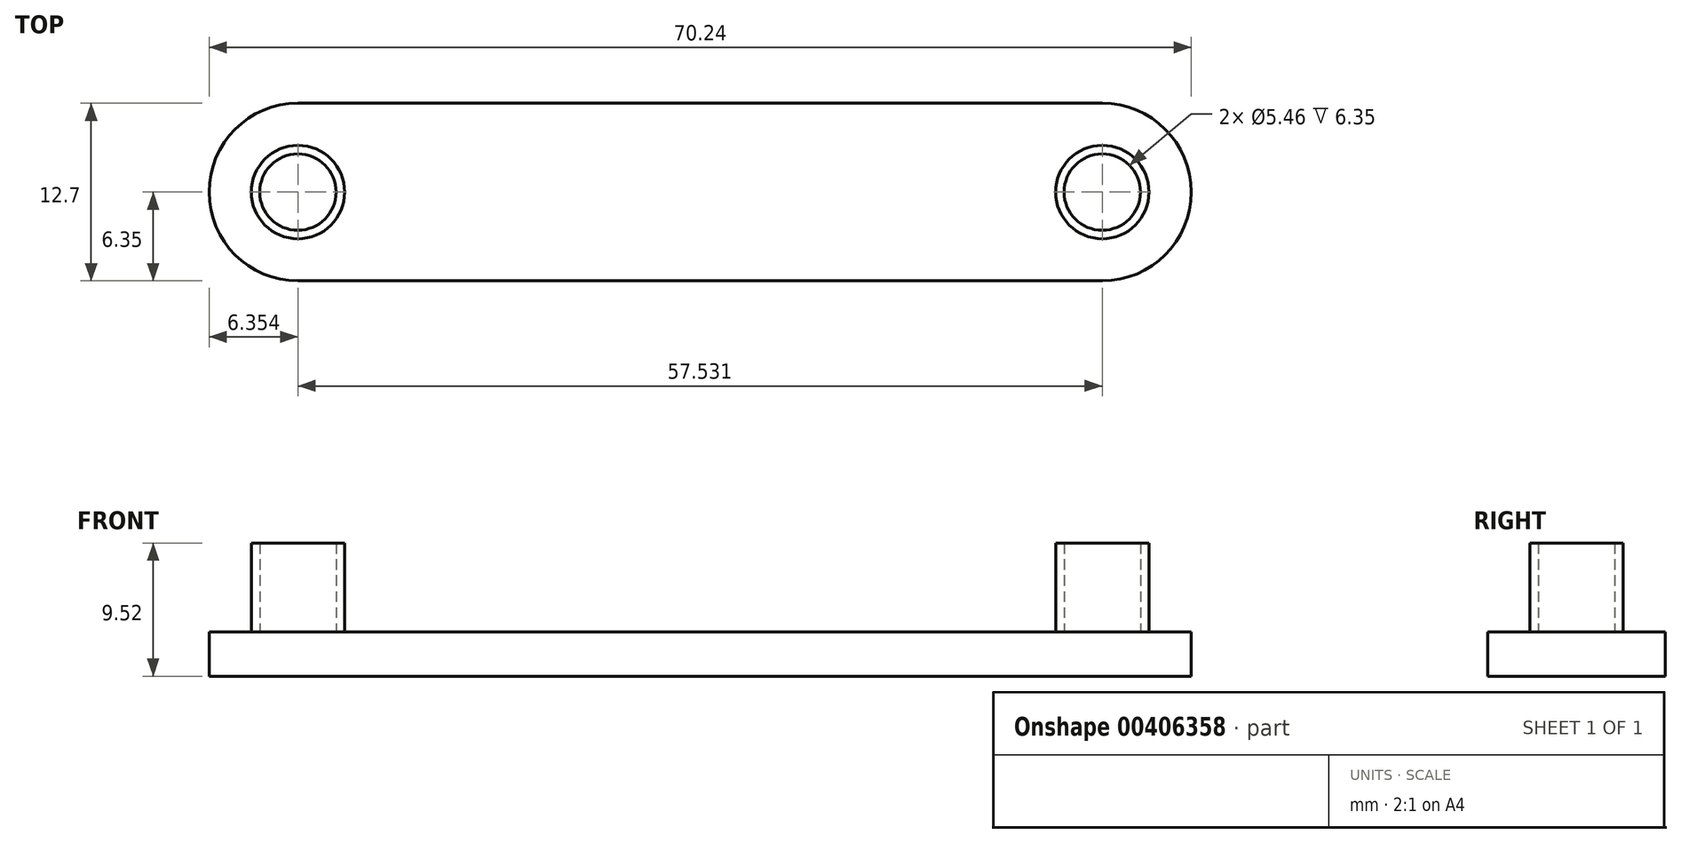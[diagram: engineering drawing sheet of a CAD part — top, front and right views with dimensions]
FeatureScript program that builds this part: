
annotation { "Feature Type Name" : "Feature", "Feature Type Description" : "" }
export const myFeature = defineFeature(function(context is Context, id is Id, definition is map)
    precondition{}
    {
        {
            var Q0;
            Q0=qCreatedBy(makeId("Top.planeOp"),FACE);
            var sketch = newSketch(context, id + "F0", { "sketchPlane" : qUnion([Q0])});
            skCircle(sketch, "E0", {"center": v(-28.77, 0) * mm, "radius": 2.73 * mm});
            skCircle(sketch, "E1", {"center": v(28.77, 0) * mm, "radius": 2.73 * mm});
            skCircle(sketch, "E2", {"center": v(-28.77, 0) * mm, "radius": 3.34 * mm});
            skCircle(sketch, "E3", {"center": v(28.77, 0) * mm, "radius": 3.34 * mm});
            skSolve(sketch);
        }
        {
            var Q0;
            Q0=makeQuery(id+"F0.imprint","IMPRINT",FACE,{"disambiguationData":[TD([[makeQuery(id+"F0.imprint","IMPRINT",EDGE,{"derivedFrom":sQuery(id+"F0.wireOp",EDGE,"E0")}),-1.0]])]});
            var Q1;
            Q1=makeQuery(id+"F0.imprint","IMPRINT",FACE,{"disambiguationData":[TD([[makeQuery(id+"F0.imprint","IMPRINT",EDGE,{"derivedFrom":sQuery(id+"F0.wireOp",EDGE,"E1")}),-1.0]])]});
            extrude(context, id + "F1", {"entities" : qUnion([Q0, Q1]), "depth" : 6.35 * mm});
        }
        {
            var Q0;
            Q0=qCreatedBy(makeId("Top.planeOp"),FACE);
            var sketch = newSketch(context, id + "F2", { "sketchPlane" : qUnion([Q0])});
            skLineSegment(sketch, "E4.bottom", {"start": v(-28.77, 6.35) * mm, "end": v(28.77, 6.35) * mm});
            skLineSegment(sketch, "E4.top", {"start": v(-28.77, -6.35) * mm, "end": v(28.77, -6.35) * mm});
            skLineSegment(sketch, "E4.left", {"start": v(-28.77, 6.35) * mm, "end": v(-28.77, -6.35) * mm, "construction": true});
            skLineSegment(sketch, "E4.right", {"start": v(28.77, 6.35) * mm, "end": v(28.77, -6.35) * mm, "construction": true});
            skArc(sketch, "E5", {"start": v(-28.77, 6.35) * mm, "mid": v(-35.12, 0) * mm, "end": v(-28.77, -6.35) * mm});
            skArc(sketch, "E6", {"start": v(28.77, -6.35) * mm, "mid": v(35.12, 0) * mm, "end": v(28.77, 6.35) * mm});
            skCircle(sketch, "E7.0", {"center": v(-28.77, 0) * mm, "radius": 2.73 * mm, "construction": true});
            skCircle(sketch, "E8.0", {"center": v(28.77, 0) * mm, "radius": 2.73 * mm, "construction": true});
            skSolve(sketch);
        }
        {
            var Q0;
            {var subQ0=sQuery(id+"F2.wireOp",EDGE,"E5");Q0=makeQuery(id+"F2.imprint","IMPRINT",FACE,{"disambiguationData":[TD([[makeQuery(id+"F2.imprint","IMPRINT",EDGE,{"derivedFrom":subQ0}),1.0]])]});}
            var Q1;
            {var subQ0=sQuery(id+"F2.wireOp",EDGE,"E7.0");var subQ1=sQuery(id+"F2.wireOp",EDGE,"E4.left");var subQ2=makeQuery(id+"F2.imprint","INTERSECT",VERTEX,{"disambiguationData":[OD(0.0)],"derivedFrom":[subQ1,subQ0]});Q1=makeQuery(id+"F2.imprint","IMPRINT",FACE,{"disambiguationData":[TD([[makeQuery(id+"F2.imprint","IMPRINT",EDGE,{"disambiguationData":[TD([[subQ2,-1.0]])],"derivedFrom":subQ1}),1.0]])]});}
            var Q2;
            {var subQ0=sQuery(id+"F2.wireOp",EDGE,"E7.0");var subQ1=sQuery(id+"F2.wireOp",EDGE,"E4.left");var subQ2=makeQuery(id+"F2.imprint","INTERSECT",VERTEX,{"disambiguationData":[OD(0.0)],"derivedFrom":[subQ1,subQ0]});Q2=makeQuery(id+"F2.imprint","IMPRINT",FACE,{"disambiguationData":[TD([[makeQuery(id+"F2.imprint","IMPRINT",EDGE,{"disambiguationData":[TD([[subQ2,-1.0]])],"derivedFrom":subQ1}),-1.0]])]});}
            var Q3;
            {var subQ5=sQuery(id+"F2.wireOp",EDGE,"E4.bottom");Q3=makeQuery(id+"F2.imprint","IMPRINT",FACE,{"disambiguationData":[TD([[makeQuery(id+"F2.imprint","IMPRINT",EDGE,{"derivedFrom":subQ5}),-1.0]])]});}
            var Q4;
            {var subQ0=sQuery(id+"F2.wireOp",EDGE,"E8.0");var subQ1=sQuery(id+"F2.wireOp",EDGE,"E4.right");var subQ2=makeQuery(id+"F2.imprint","INTERSECT",VERTEX,{"disambiguationData":[OD(0.0)],"derivedFrom":[subQ1,subQ0]});Q4=makeQuery(id+"F2.imprint","IMPRINT",FACE,{"disambiguationData":[TD([[makeQuery(id+"F2.imprint","IMPRINT",EDGE,{"disambiguationData":[TD([[subQ2,-1.0]])],"derivedFrom":subQ1}),1.0]])]});}
            var Q5;
            {var subQ0=sQuery(id+"F2.wireOp",EDGE,"E8.0");var subQ1=sQuery(id+"F2.wireOp",EDGE,"E4.right");var subQ2=makeQuery(id+"F2.imprint","INTERSECT",VERTEX,{"disambiguationData":[OD(0.0)],"derivedFrom":[subQ1,subQ0]});Q5=makeQuery(id+"F2.imprint","IMPRINT",FACE,{"disambiguationData":[TD([[makeQuery(id+"F2.imprint","IMPRINT",EDGE,{"disambiguationData":[TD([[subQ2,-1.0]])],"derivedFrom":subQ1}),-1.0]])]});}
            var Q6;
            {var subQ0=sQuery(id+"F2.wireOp",EDGE,"E6");Q6=makeQuery(id+"F2.imprint","IMPRINT",FACE,{"disambiguationData":[TD([[makeQuery(id+"F2.imprint","IMPRINT",EDGE,{"derivedFrom":subQ0}),1.0]])]});}
            extrude(context, id + "F3", {"entities" : qUnion([Q0, Q1, Q2, Q3, Q4, Q5, Q6]), "oppositeDirection" : true, "depth" : 3.17 * mm});
        }
    });
